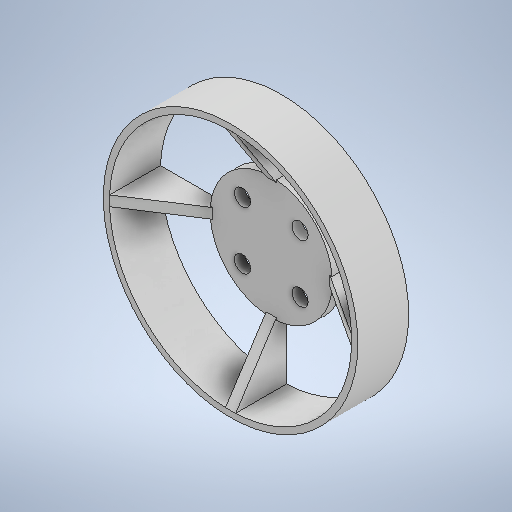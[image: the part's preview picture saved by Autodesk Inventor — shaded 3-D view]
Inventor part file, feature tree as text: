
AUTODESK INVENTOR PART (.ipt)
format: ipt  version: 2025.3 (Build 293356000, 356)  size: 313,344 bytes
history: native  units: mm
features: sketch x4, extrude x3, other x1, pattern_circular x1, hole x1
ambient origin geometry x8: Origin, YZ Plane, XZ Plane, XY Plane, X Axis, Y Axis, Z Axis, Center Point
bodies: Body1 (feature_tree)
feature tree (10):
  other  "ソリッド1"
  extrude  "ハブ"  Depth=24.0mm
  extrude  "リム"  Depth=2.0mm TaperAngle=0.0deg
  extrude  "スポーク"  Depth=50.0mm
  pattern_circular  "円形状パターン1"  [2 undecoded]
  hole  "穴1"  [1 undecoded]
  sketch  "スケッチ1"
  sketch  "スケッチ2"
  sketch  "スケッチ5"
  sketch  "スケッチ6"
note: 3 required parameter values undecoded (feature->parameter linkage not recoverable at this tier; creation-order binding heuristic only, values carry confidence <= 0.55)
